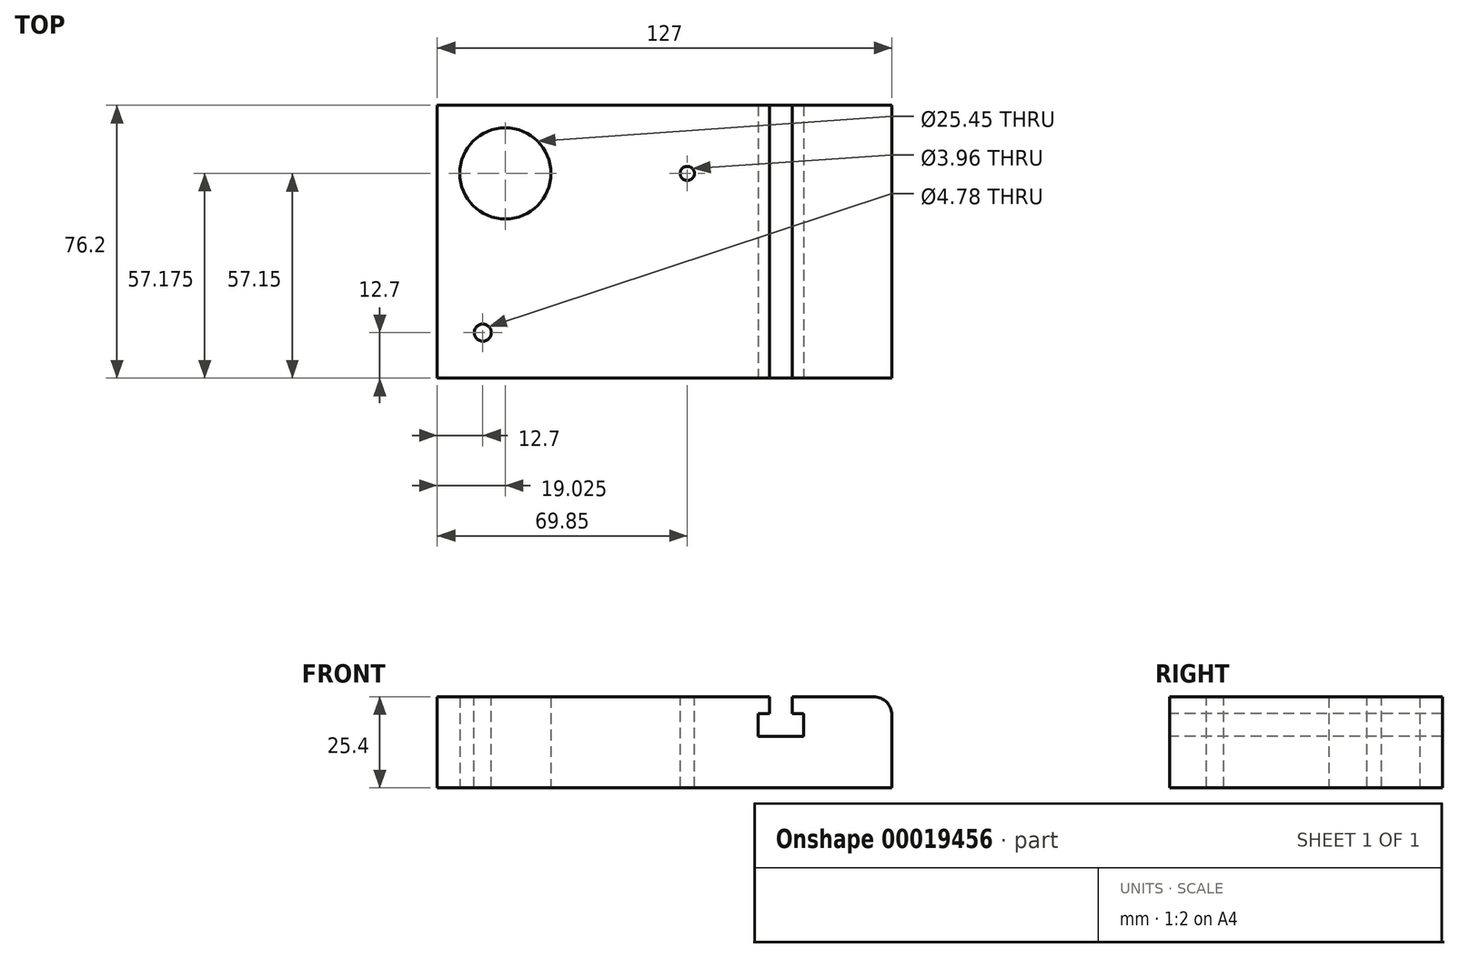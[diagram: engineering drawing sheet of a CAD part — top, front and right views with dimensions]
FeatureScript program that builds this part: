
annotation { "Feature Type Name" : "Feature", "Feature Type Description" : "" }
export const myFeature = defineFeature(function(context is Context, id is Id, definition is map)
    precondition{}
    {
        {
            var Q0;
            Q0=qCreatedBy(makeId("Top.planeOp"),FACE);
            var sketch = newSketch(context, id + "F0", { "sketchPlane" : qUnion([Q0])});
            skLineSegment(sketch, "E0.bottom", {"start": v(-63.5, 38.1) * mm, "end": v(63.5, 38.1) * mm});
            skLineSegment(sketch, "E0.top", {"start": v(-63.5, -38.1) * mm, "end": v(63.5, -38.1) * mm});
            skLineSegment(sketch, "E0.left", {"start": v(-63.5, 38.1) * mm, "end": v(-63.5, -38.1) * mm});
            skLineSegment(sketch, "E0.right", {"start": v(63.5, 38.1) * mm, "end": v(63.5, -38.1) * mm});
            skLineSegment(sketch, "E1", {"start": v(0, 0) * mm, "end": v(63.5, 0) * mm, "construction": true});
            skLineSegment(sketch, "E2", {"start": v(0, 0) * mm, "end": v(0, 38.1) * mm, "construction": true});
            skCircle(sketch, "E3", {"center": v(-44.48, 19.08) * mm, "radius": 12.73 * mm});
            skSolve(sketch);
        }
        {
            var Q0;
            Q0 = qSketchRegion(id + "F0", true);
            extrude(context, id + "F1", {"entities" : qUnion([Q0]), "endBound" : BoundingType.SYMMETRIC, "depth" : 25.4 * mm});
        }
        {
            var Q0;
            Q0=makeQuery(id+"F1.opExtrude","CAP_FACE",FACE,{"disambiguationData":[OSD([sQuery(id+"F0.wireOp",EDGE,"E0.bottom"),sQuery(id+"F0.wireOp",EDGE,"E0.top"),sQuery(id+"F0.wireOp",EDGE,"E0.left"),sQuery(id+"F0.wireOp",EDGE,"E0.right"),sQuery(id+"F0.wireOp",EDGE,"E3")])],"isStart":false});
            var sketch = newSketch(context, id + "F2", { "sketchPlane" : qUnion([Q0])});
            skPoint(sketch, "E4", {"position": v(6.35, 19.05) * mm});
            skSolve(sketch);
        }
        {
            var Q0;
            Q0=sQuery(id+"F2.wireOp",VERTEX,"E4");
            var Q1;
            Q1=makeQuery(id+"F1.opExtrude","SWEPT_BODY",BODY,{"disambiguationData":[OSD([sQuery(id+"F0.wireOp",EDGE,"E0.bottom"),sQuery(id+"F0.wireOp",EDGE,"E0.top"),sQuery(id+"F0.wireOp",EDGE,"E0.left"),sQuery(id+"F0.wireOp",EDGE,"E0.right"),sQuery(id+"F0.wireOp",EDGE,"E3")])]});
            hole(context, id + "F3", {"style" : HoleStyle.SIMPLE, "holeDiameter" : 3.96 * mm, "endStyle" : HoleEndStyle.THROUGH, "locations" : qUnion([Q0]), "scope" : qUnion([Q1])});
        }
        {
            var Q0;
            Q0=makeQuery(id+"F1.opExtrude","CAP_EDGE",EDGE,{"disambiguationData":[OSD([sQuery(id+"F0.wireOp",EDGE,"E0.right")])],"isStart":false});
            fillet(context, id + "F4", {"entities" : qUnion([Q0]), "radius" : 5.08 * mm, "tangentPropagation" : true, "allowEdgeOverflow" : false});
        }
        {
            var Q0;
            Q0=makeQuery(id+"F1.opExtrude","SWEPT_FACE",FACE,{"disambiguationData":[OSD([sQuery(id+"F0.wireOp",EDGE,"E0.top")])]});
            var sketch = newSketch(context, id + "F5", { "sketchPlane" : qUnion([Q0])});
            skLineSegment(sketch, "E5.bottom", {"start": v(29.25, 12.7) * mm, "end": v(35.6, 12.7) * mm});
            skLineSegment(sketch, "E5.top", {"start": v(29.25, 7.94) * mm, "end": v(35.6, 7.94) * mm});
            skLineSegment(sketch, "E5.left", {"start": v(29.25, 12.7) * mm, "end": v(29.25, 7.94) * mm});
            skLineSegment(sketch, "E5.right", {"start": v(35.6, 12.7) * mm, "end": v(35.6, 7.94) * mm});
            skLineSegment(sketch, "E6.bottom", {"start": v(26.08, 7.94) * mm, "end": v(38.78, 7.94) * mm});
            skLineSegment(sketch, "E6.top", {"start": v(26.08, 1.59) * mm, "end": v(38.78, 1.59) * mm});
            skLineSegment(sketch, "E6.left", {"start": v(26.08, 7.94) * mm, "end": v(26.08, 1.59) * mm});
            skLineSegment(sketch, "E6.right", {"start": v(38.78, 7.94) * mm, "end": v(38.78, 1.59) * mm});
            skPoint(sketch, "E7", {"position": v(32.43, 7.94) * mm});
            skSolve(sketch);
        }
        {
            var Q0;
            Q0 = qSketchRegion(id + "F5", true);
            extrude(context, id + "F6", {"entities" : qUnion([Q0]), "operationType" : NewBodyOperationType.REMOVE, "endBound" : BoundingType.THROUGH_ALL, "oppositeDirection" : true, "depth" : 25.4 * mm});
        }
        {
            var Q0;
            {var subQ0=sQuery(id+"F0.wireOp",EDGE,"E0.bottom");var subQ1=sQuery(id+"F0.wireOp",EDGE,"E0.top");var subQ2=sQuery(id+"F0.wireOp",EDGE,"E0.left");var subQ3=sQuery(id+"F0.wireOp",EDGE,"E3");Q0=makeQuery(id+"F6.boolean.opBoolean","SPLIT",FACE,{"disambiguationData":[TD([makeQuery(id+"F1.opExtrude","SWEPT_FACE",FACE,{"disambiguationData":[OSD([subQ2])]})])],"derivedFrom":makeQuery(id+"F1.opExtrude","CAP_FACE",FACE,{"disambiguationData":[OSD([subQ0,subQ1,subQ2,sQuery(id+"F0.wireOp",EDGE,"E0.right"),subQ3])],"isStart":false})});}
            var sketch = newSketch(context, id + "F7", { "sketchPlane" : qUnion([Q0])});
            skPoint(sketch, "E8", {"position": v(-50.8, -25.4) * mm});
            skSolve(sketch);
        }
        {
            var Q0;
            Q0=sQuery(id+"F7.wireOp",VERTEX,"E8");
            var Q1;
            Q1=makeQuery(id+"F1.opExtrude","SWEPT_BODY",BODY,{"disambiguationData":[OSD([sQuery(id+"F0.wireOp",EDGE,"E0.bottom"),sQuery(id+"F0.wireOp",EDGE,"E0.top"),sQuery(id+"F0.wireOp",EDGE,"E0.left"),sQuery(id+"F0.wireOp",EDGE,"E0.right"),sQuery(id+"F0.wireOp",EDGE,"E3")])]});
            hole(context, id + "F8", {"style" : HoleStyle.SIMPLE, "holeDiameter" : 4.78 * mm, "endStyle" : HoleEndStyle.THROUGH, "locations" : qUnion([Q0]), "scope" : qUnion([Q1])});
        }
    });
